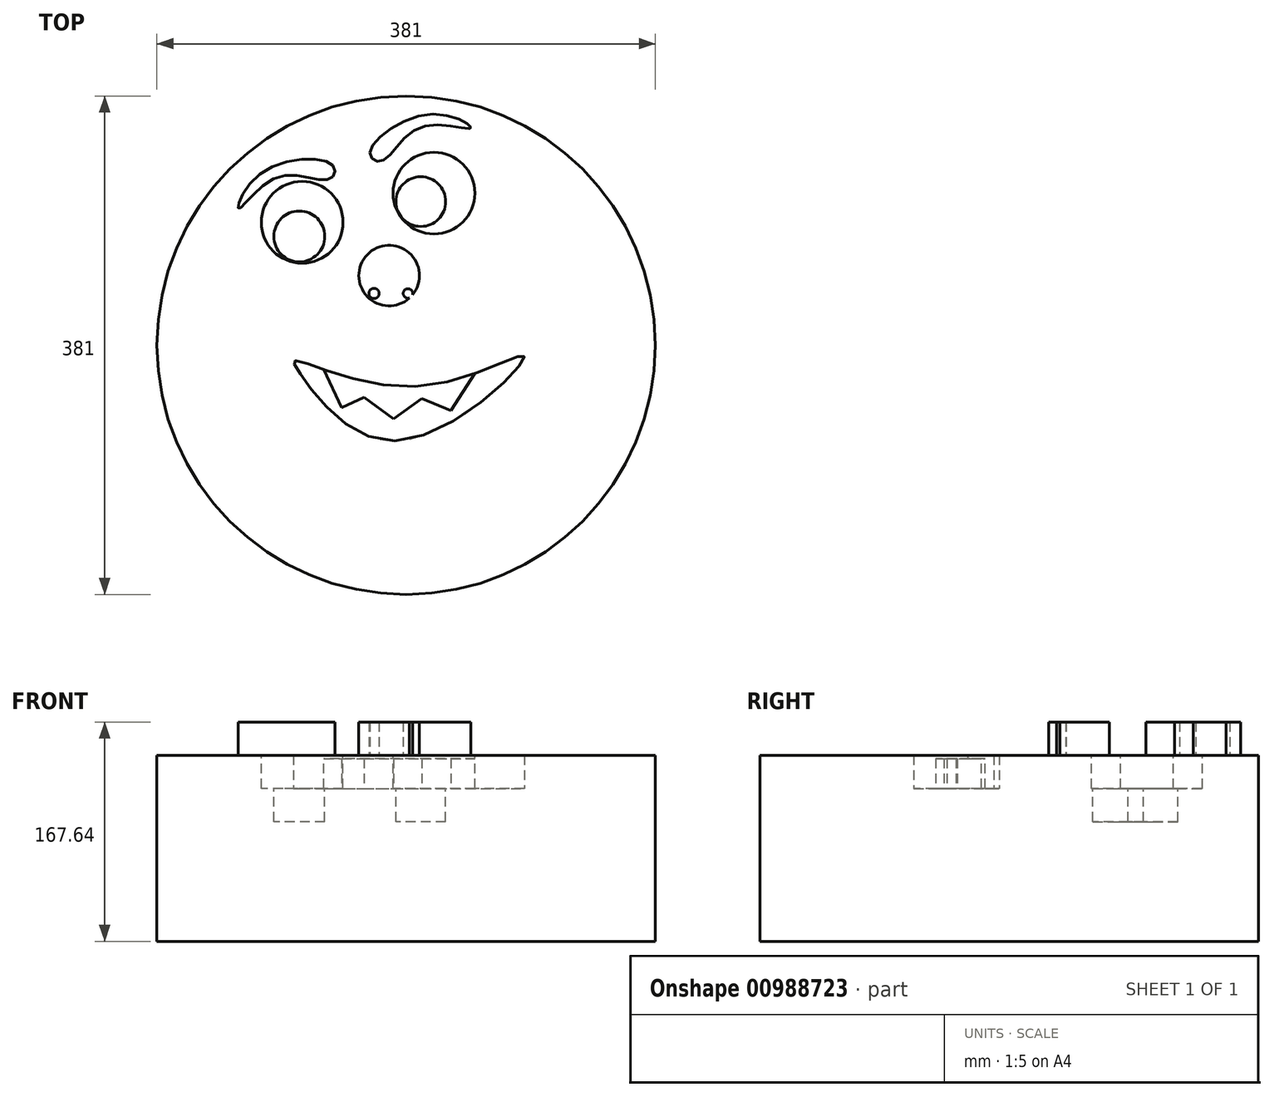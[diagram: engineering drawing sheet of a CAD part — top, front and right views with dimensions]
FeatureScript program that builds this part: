
annotation { "Feature Type Name" : "Feature", "Feature Type Description" : "" }
export const myFeature = defineFeature(function(context is Context, id is Id, definition is map)
    precondition{}
    {
        {
            var Q0;
            Q0=qCreatedBy(makeId("Top.planeOp"),FACE);
            var sketch = newSketch(context, id + "F0", { "sketchPlane" : qUnion([Q0])});
            skCircle(sketch, "E0", {"center": v(-34.1, 31.51) * mm, "radius": 190.5 * mm});
            skSolve(sketch);
        }
        {
            var Q0;
            Q0 = qSketchRegion(id + "F0", true);
            extrude(context, id + "F1", {"entities" : qUnion([Q0]), "depth" : 142.24 * mm, "offsetDistance" : 25.4 * mm});
        }
        {
            var Q0;
            Q0=makeQuery(id+"F1.opExtrude","CAP_FACE",FACE,{"disambiguationData":[OSD([sQuery(id+"F0.wireOp",EDGE,"E0")])],"isStart":false});
            var sketch = newSketch(context, id + "F2", { "sketchPlane" : qUnion([Q0])});
            skCircle(sketch, "E1", {"center": v(-113.61, 125.41) * mm, "radius": 31.24 * mm});
            skCircle(sketch, "E2", {"center": v(-12.88, 147.72) * mm, "radius": 31.24 * mm});
            skSolve(sketch);
        }
        {
            var Q0;
            Q0 = qSketchRegion(id + "F2", true);
            extrude(context, id + "F3", {"entities" : qUnion([Q0]), "operationType" : NewBodyOperationType.REMOVE, "oppositeDirection" : true, "depth" : 25.4 * mm, "offsetDistance" : 25.4 * mm});
        }
        {
            var Q0;
            Q0=makeQuery(id+"F1.opExtrude","CAP_FACE",FACE,{"disambiguationData":[OSD([sQuery(id+"F0.wireOp",EDGE,"E0")])],"isStart":false});
            var sketch = newSketch(context, id + "F4", { "sketchPlane" : qUnion([Q0])});
            skFitSpline(sketch, "E3", {"points": [v(-115.05, 9.57) * mm, v(-39.5, -41.52) * mm, v(56.2, 22.52) * mm, v(-25.11, 0) * mm, v(-119.37, 19.64) * mm, v(-115.05, 9.57) * mm]});
            skSolve(sketch);
        }
        {
            var Q0;
            Q0 = qSketchRegion(id + "F4", true);
            extrude(context, id + "F5", {"entities" : qUnion([Q0]), "operationType" : NewBodyOperationType.REMOVE, "oppositeDirection" : true, "depth" : 25.4 * mm, "offsetDistance" : 25.4 * mm});
        }
        {
            var Q0;
            Q0=makeQuery(id+"F5.boolean.opBoolean","COPY",FACE,{"derivedFrom":makeQuery(id+"F5.opExtrude","CAP_FACE",FACE,{"disambiguationData":[OSD([sQuery(id+"F4.wireOp",EDGE,"E3")])],"isStart":false})});
            var sketch = newSketch(context, id + "F6", { "sketchPlane" : qUnion([Q0])});
            skLineSegment(sketch, "E4", {"start": v(-102.82, 25.4) * mm, "end": v(-83.4, -16.33) * mm});
            skLineSegment(sketch, "E5", {"start": v(-83.4, -16.33) * mm, "end": v(-66.25, -8.35) * mm});
            skLineSegment(sketch, "E6", {"start": v(-66.25, -8.35) * mm, "end": v(-43.82, -24.97) * mm});
            skLineSegment(sketch, "E7", {"start": v(-43.82, -24.97) * mm, "end": v(-22.23, -9.14) * mm});
            skLineSegment(sketch, "E8", {"start": v(-22.23, -9.14) * mm, "end": v(0, -18.5) * mm});
            skLineSegment(sketch, "E9", {"start": v(0, -18.5) * mm, "end": v(25.25, 20.36) * mm});
            skLineSegment(sketch, "E10", {"start": v(25.25, 20.36) * mm, "end": v(-102.82, 25.4) * mm});
            skSolve(sketch);
        }
        {
            var Q0;
            Q0 = qSketchRegion(id + "F6", true);
            extrude(context, id + "F7", {"entities" : qUnion([Q0]), "operationType" : NewBodyOperationType.ADD, "depth" : 22.86 * mm, "offsetDistance" : 25.4 * mm});
        }
        {
            var Q0;
            Q0=makeQuery(id+"F3.boolean.opBoolean","COPY",FACE,{"derivedFrom":makeQuery(id+"F3.opExtrude","CAP_FACE",FACE,{"disambiguationData":[OSD([sQuery(id+"F2.wireOp",EDGE,"E1")])],"isStart":false})});
            var sketch = newSketch(context, id + "F8", { "sketchPlane" : qUnion([Q0])});
            skCircle(sketch, "E11", {"center": v(-115.77, 114.62) * mm, "radius": 19.44 * mm});
            skCircle(sketch, "E12", {"center": v(-22.95, 141.24) * mm, "radius": 19 * mm});
            skSolve(sketch);
        }
        {
            var Q0;
            Q0=makeQuery(id+"F1.opExtrude","CAP_FACE",FACE,{"disambiguationData":[OSD([sQuery(id+"F0.wireOp",EDGE,"E0")])],"isStart":false});
            var sketch = newSketch(context, id + "F9", { "sketchPlane" : qUnion([Q0])});
            skCircle(sketch, "E13", {"center": v(-47.17, 84.72) * mm, "radius": 23.14 * mm});
            skSolve(sketch);
        }
        {
            var Q0;
            Q0=makeQuery(id+"F9.imprint","IMPRINT",FACE,{"disambiguationData":[TD([[makeQuery(id+"F9.imprint","IMPRINT",EDGE,{"derivedFrom":sQuery(id+"F9.wireOp",EDGE,"E13")}),1.0]])]});
            var sketch = newSketch(context, id + "F10", { "sketchPlane" : qUnion([Q0])});
            skCircle(sketch, "E14", {"center": v(-58.72, 71.02) * mm, "radius": 3.87 * mm});
            skCircle(sketch, "E15", {"center": v(-32.74, 71.02) * mm, "radius": 3.64 * mm});
            skSolve(sketch);
        }
        {
            var Q0;
            Q0 = qSketchRegion(id + "F9", true);
            extrude(context, id + "F11", {"entities" : qUnion([Q0]), "operationType" : NewBodyOperationType.ADD, "depth" : 25.4 * mm, "offsetDistance" : 25.4 * mm});
        }
        {
            var Q0;
            Q0 = qSketchRegion(id + "F10", true);
            var Q1;
            Q1=makeQuery(id+"F11.opExtrude","CAP_FACE",FACE,{"disambiguationData":[OSD([sQuery(id+"F9.wireOp",EDGE,"E13")])],"isStart":false});
            extrude(context, id + "F12", {"entities" : qUnion([Q0, Q1]), "operationType" : NewBodyOperationType.REMOVE, "depth" : 25.4 * mm, "offsetDistance" : 25.4 * mm});
        }
        {
            var Q0;
            Q0=makeQuery(id+"F8.imprint","IMPRINT",FACE,{"disambiguationData":[TD([[makeQuery(id+"F8.imprint","IMPRINT",EDGE,{"derivedFrom":sQuery(id+"F8.wireOp",EDGE,"E11")}),1.0]])]});
            var Q1;
            Q1=makeQuery(id+"F8.imprint","IMPRINT",FACE,{"disambiguationData":[TD([[makeQuery(id+"F8.imprint","IMPRINT",EDGE,{"derivedFrom":sQuery(id+"F8.wireOp",EDGE,"E12")}),1.0]])]});
            extrude(context, id + "F13", {"entities" : qUnion([Q0, Q1]), "operationType" : NewBodyOperationType.REMOVE, "oppositeDirection" : true, "depth" : 25.4 * mm, "offsetDistance" : 25.4 * mm});
        }
        {
            var Q0;
            Q0=makeQuery(id+"F12.boolean.opBoolean","MERGE",FACE,{"derivedFrom":[makeQuery(id+"F1.opExtrude","CAP_FACE",FACE,{"disambiguationData":[OSD([sQuery(id+"F0.wireOp",EDGE,"E0")])],"isStart":false})],"fromTools":[makeQuery(id+"F12.opExtrude","CAP_FACE",FACE,{"disambiguationData":[OSD([sQuery(id+"F10.wireOp",EDGE,"E15")])],"isStart":true})]});
            var sketch = newSketch(context, id + "F14", { "sketchPlane" : qUnion([Q0])});
            skFitSpline(sketch, "E16", {"points": [v(-61.8, 178.66) * mm, v(-13.6, 208.16) * mm, v(15.18, 197.36) * mm, v(-22.95, 198.08) * mm, v(-53.17, 172.18) * mm, v(-61.8, 178.66) * mm]});
            skLineSegment(sketch, "E17", {"start": v(-89.76, 213.7) * mm, "end": v(35.13, -145.96) * mm});
            skFitSpline(sketch, "E18.MirrorC", {"points": [v(-89.98, 168.87) * mm, v(-146.1, 162.15) * mm, v(-162, 135.84) * mm, v(-132.51, 160.04) * mm, v(-92.74, 158.44) * mm, v(-89.98, 168.87) * mm]});
            skSolve(sketch);
        }
        {
            var Q0;
            Q0=makeQuery(id+"F14.imprint","IMPRINT",FACE,{"disambiguationData":[TD([[makeQuery(id+"F14.imprint","IMPRINT",EDGE,{"derivedFrom":sQuery(id+"F14.wireOp",EDGE,"E16")}),-1.0]])]});
            var Q1;
            Q1=makeQuery(id+"F14.imprint","IMPRINT",FACE,{"disambiguationData":[TD([[makeQuery(id+"F14.imprint","IMPRINT",EDGE,{"derivedFrom":sQuery(id+"F14.wireOp",EDGE,"E18.MirrorC")}),1.0]])]});
            extrude(context, id + "F15", {"entities" : qUnion([Q0, Q1]), "operationType" : NewBodyOperationType.ADD, "depth" : 25.4 * mm, "offsetDistance" : 25.4 * mm});
        }
    });
